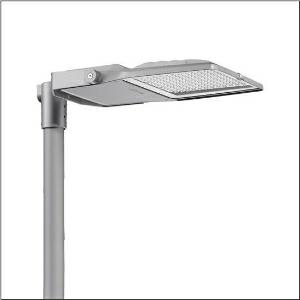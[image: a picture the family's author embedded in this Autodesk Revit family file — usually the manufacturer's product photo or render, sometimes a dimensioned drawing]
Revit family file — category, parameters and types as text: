
# Revit family: floodlight_fl_21_iq_midi___pl33t_5xa7782e2f3a_552b
name_source: partatom
category: Lighting Fixtures
units: mm (PartAtom-declared; Revit-internal decimal feet)

## family parameters
Cut with Voids When Loaded = No
Host = Face
Light Source = No
Part Type = Normal
Room Calculation Point = No
Round Connector Dimension = Use Diameter
Shared = No

## types (1)
- --- (1 x LED, 26540 lm, 208.1 W, 3000K)
    Apparent Load = 208 VA
    CIE Flux Codes = 26 75 99 100 100
    Color Rendering = 70
    Color Temperature = 3000K
    Default Elevation = 1800 mm
    Description = Floodlight FL 21 iQ midi, floodlight, primary light control with lens, of PMMA, primary optical cover: protective disc, of toughened safety glass, transparent, light distribution: PL33T, light emission: direct distribution, installation type: surface-mounted, LED, High Power LED, rated luminous flux: 26.540lm, luminous efficacy: 128lm/W, light colour: 730, colour temperature: 3000K, control gear: iQ Street-Remote/DALI, control: optimised constant luminous flux control (CLO 2.0), Desk-Remote (wireless, voltage-free reading and setting of iQ features in the workshop via application-optimized NFC function/RFID function), Smart-Wire, Night-Set, Temp-Guard, Auto-Match, Street-Remote, with terminal, 6-pole, mains connection: 220..240V, AC, 50/60Hz, start of lifetime: 208W, end of service life: 227W, reduction: 90W, luminaire housing, of diecast aluminium, powder-coated, Siteco® metallic grey (DB 702S), corrosivity category C5 mid according to DIN EN ISO 12944, suitable for swimming pools, chlorine-resistant, sealing non-destructively replaceable, please order mast flange separately, mast bracket, of steel, galvanised, powder-coated, Siteco® metallic grey (DB 702S), protection rating (complete): IP66, insulation class (complete): insulation class II (safety insulation), certification: CE, ENEC, VDE, protection symbol: D, impact resistance: IK08, permissible operating ambient temperature: -40..+40°C, permissible operating ambient temperature for outdoor applications: -40..+50°C, standard: DIN EN 12944, LABS conformity tested according to VDMA 24364:2018-05, packaging unit: 1 piece

Light Distribution: PL33T
    Height = 76 mm
    Lamp = 1 x LED
    Lamp Light Flux = 26540 lm
    Lamp Power = 208.1 W
    Lamp count = 1
    Length = 657 mm
    Luminous efficacy = 128 lm/W
    Manufacturer = Siteco
    ModVariant = No
    Model = 5XA7782E2F3A
    Number of Poles = 1
    OnlyDefault = Yes
    Power Factor = 1
    Product Name = Floodlight FL 21 iQ midi | PL33T
    Product group = floodlight | pylon annexe
    ProductGroupID = 6200
    Protection Class = Protection class II
    Protection Degree = IP 66
    RLX_Detail_Level = 1
    RLX_Emergency_Light_Flux = 0 lm
    RLX_Emergency_Type = 0
    RLX_Emergency_Type_DB = No
    RlxData = <blob elided: 153833 chars, md5=48197787>
    Socket = socket
    Standby Power = 0 W
    System Light Flux = 26540 lm
    System Power = 208 W
    Type Comments = factory setting: luminous flux: 100 % | dim-lin: 254 | 710 mA
    Type Image = l_1007123.jpg
    URL = http://relux.com
    VarID = @adj_103830
    Voltage = 0 V
    Weight = 0.00 kg
    Width = 442 mm

## geometry (parser evidence)
native form markers: Blend x4, Sweep x12
no freeform markers — native parametric forms only
